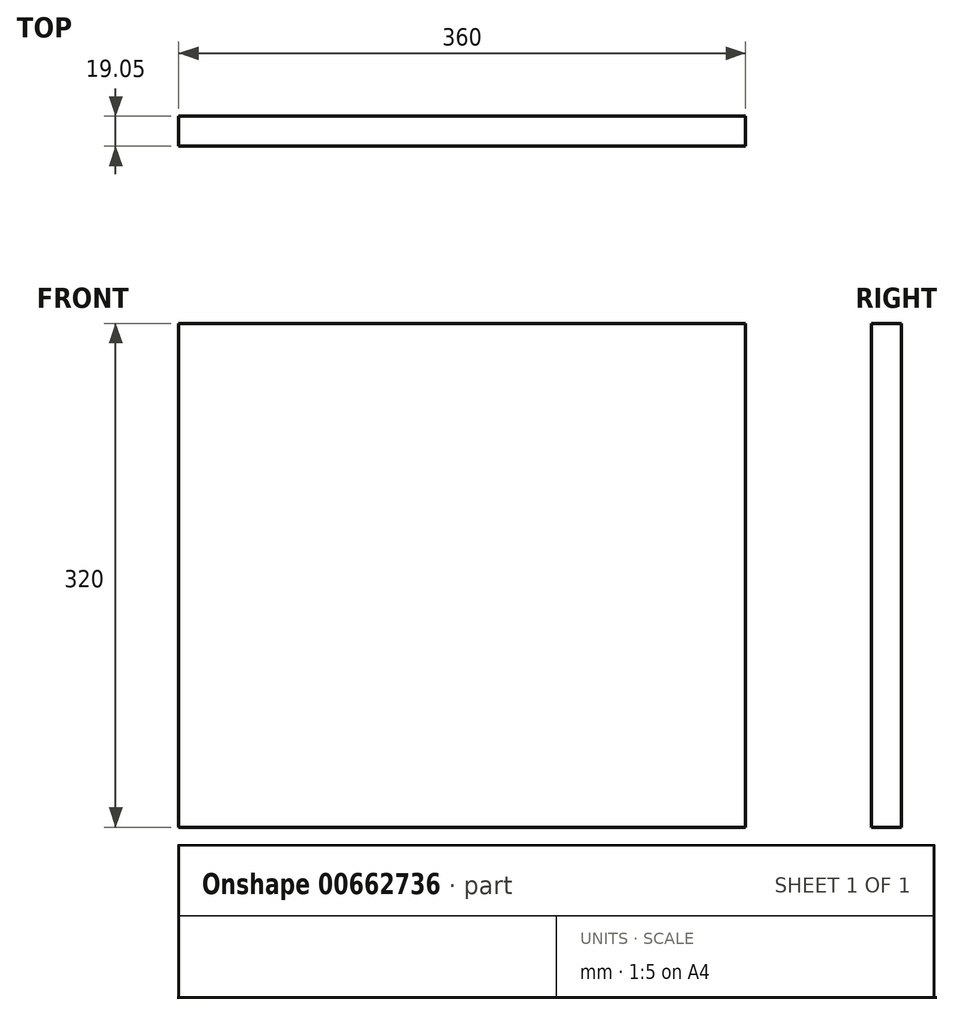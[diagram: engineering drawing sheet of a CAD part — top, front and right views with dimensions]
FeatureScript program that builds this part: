
annotation { "Feature Type Name" : "Feature", "Feature Type Description" : "" }
export const myFeature = defineFeature(function(context is Context, id is Id, definition is map)
    precondition{}
    {
        {
            var Q0;
            Q0=qCreatedBy(makeId("Front.planeOp"),FACE);
            var sketch = newSketch(context, id + "F0", { "sketchPlane" : qUnion([Q0])});
            skLineSegment(sketch, "E0.bottom", {"start": v(180, 160) * mm, "end": v(-180, 160) * mm});
            skLineSegment(sketch, "E0.top", {"start": v(180, -160) * mm, "end": v(-180, -160) * mm});
            skLineSegment(sketch, "E0.left", {"start": v(180, 160) * mm, "end": v(180, -160) * mm});
            skLineSegment(sketch, "E0.right", {"start": v(-180, 160) * mm, "end": v(-180, -160) * mm});
            skPoint(sketch, "E0.middle", {"position": v(0, 0) * mm});
            skSolve(sketch);
        }
        {
            var Q0;
            Q0=makeQuery(id+"F0.imprint","IMPRINT",FACE,{"disambiguationData":[TD([[makeQuery(id+"F0.imprint","IMPRINT",EDGE,{"derivedFrom":sQuery(id+"F0.wireOp",EDGE,"E0.bottom")}),1.0]])]});
            extrude(context, id + "F1", {"entities" : qUnion([Q0]), "oppositeDirection" : true, "depth" : (25.4 * .75) * mm, "offsetDistance" : 25 * mm});
        }
    });
